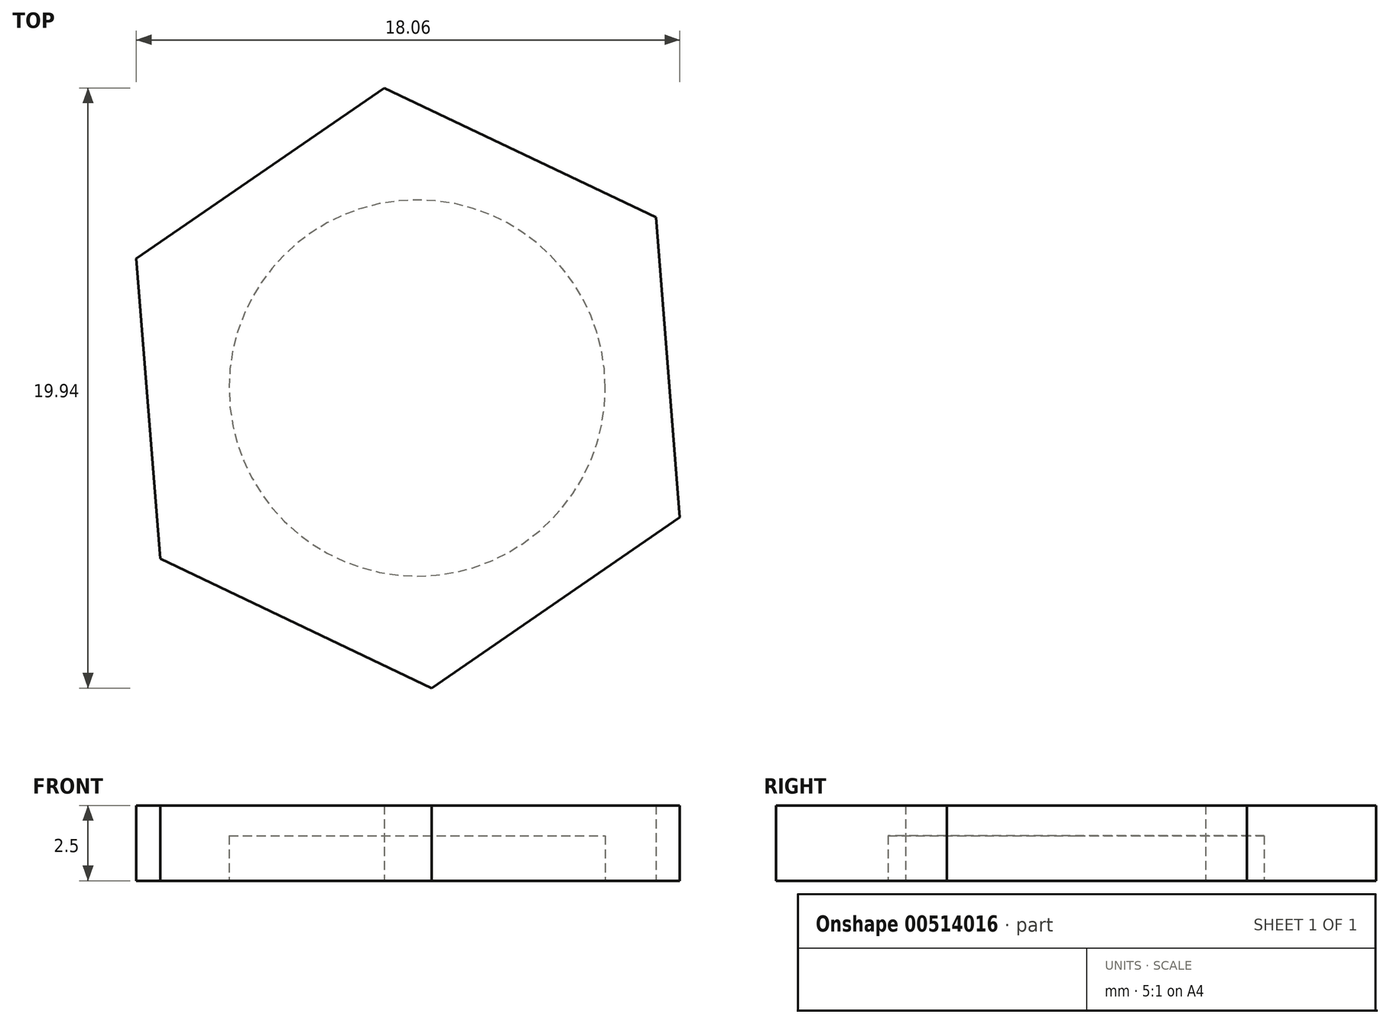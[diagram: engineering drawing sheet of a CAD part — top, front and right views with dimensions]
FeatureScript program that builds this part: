
annotation { "Feature Type Name" : "Feature", "Feature Type Description" : "" }
export const myFeature = defineFeature(function(context is Context, id is Id, definition is map)
    precondition{}
    {
        {
            var Q0;
            Q0=qCreatedBy(makeId("Top.planeOp"),FACE);
            var sketch = newSketch(context, id + "F0", { "sketchPlane" : qUnion([Q0])});
            skCircle(sketch, "E0", {"center": v(0, 0) * mm, "radius": 6.25 * mm});
            skCircle(sketch, "E1.cCircle", {"center": v(0, 0) * mm, "radius": 10 * mm, "construction": true});
            skLineSegment(sketch, "E1.0", {"start": v(8.24, 5.67) * mm, "end": v(9.03, -4.3) * mm});
            skLineSegment(sketch, "E1.1", {"start": v(9.03, -4.3) * mm, "end": v(0.79, -9.97) * mm});
            skLineSegment(sketch, "E1.2", {"start": v(0.79, -9.97) * mm, "end": v(-8.24, -5.67) * mm});
            skLineSegment(sketch, "E1.3", {"start": v(-8.24, -5.67) * mm, "end": v(-9.03, 4.3) * mm});
            skLineSegment(sketch, "E1.4", {"start": v(-9.03, 4.3) * mm, "end": v(-0.79, 9.97) * mm});
            skLineSegment(sketch, "E1.5", {"start": v(-0.79, 9.97) * mm, "end": v(8.24, 5.67) * mm});
            skSolve(sketch);
        }
        {
            var Q0;
            Q0 = qSketchRegion(id + "F0", true);
            var Q1;
            Q1=makeQuery(id+"F0.imprint","IMPRINT",FACE,{"disambiguationData":[TD([[makeQuery(id+"F0.imprint","IMPRINT",EDGE,{"derivedFrom":sQuery(id+"F0.wireOp",EDGE,"E0")}),1.0]])]});
            extrude(context, id + "F1", {"entities" : qUnion([Q0, Q1]), "depth" : 2.5 * mm});
        }
        {
            var Q0;
            Q0=makeQuery(id+"F1.opExtrude","CAP_FACE",FACE,{"disambiguationData":[OSD([sQuery(id+"F0.wireOp",EDGE,"E1.0"),sQuery(id+"F0.wireOp",EDGE,"E1.1"),sQuery(id+"F0.wireOp",EDGE,"E1.2"),sQuery(id+"F0.wireOp",EDGE,"E1.3"),sQuery(id+"F0.wireOp",EDGE,"E1.4"),sQuery(id+"F0.wireOp",EDGE,"E1.5")])],"isStart":true});
            var sketch = newSketch(context, id + "F2", { "sketchPlane" : qUnion([Q0])});
            skCircle(sketch, "E2", {"center": v(0.3, 0) * mm, "radius": 6.25 * mm});
            skSolve(sketch);
        }
        {
            var Q0;
            Q0 = qSketchRegion(id + "F2", true);
            extrude(context, id + "F3", {"entities" : qUnion([Q0]), "operationType" : NewBodyOperationType.REMOVE, "oppositeDirection" : true, "depth" : 1.5 * mm});
        }
    });
